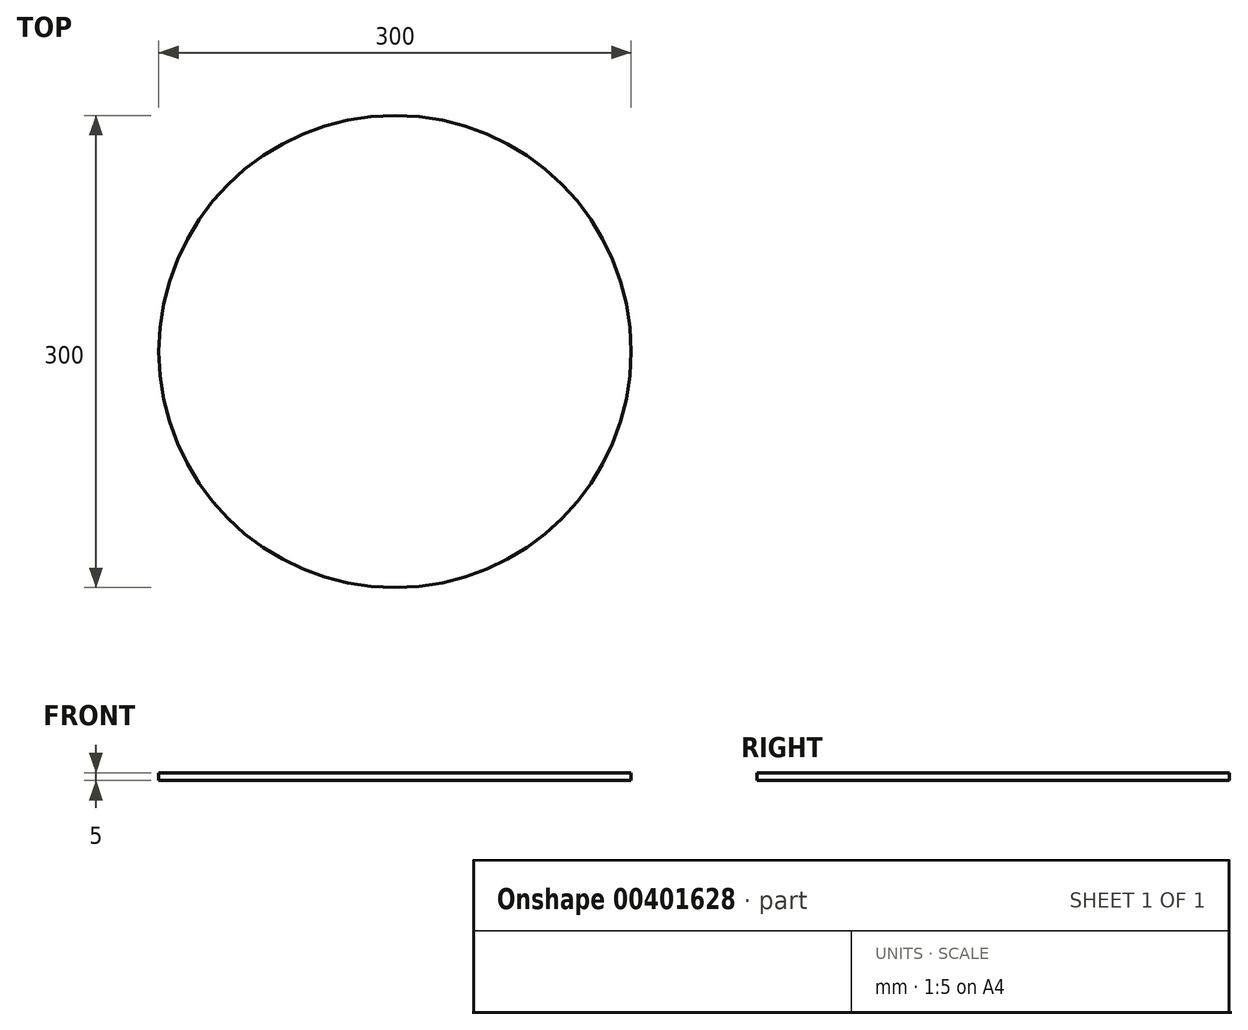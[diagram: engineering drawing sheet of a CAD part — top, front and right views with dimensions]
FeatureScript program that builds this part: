
annotation { "Feature Type Name" : "Feature", "Feature Type Description" : "" }
export const myFeature = defineFeature(function(context is Context, id is Id, definition is map)
    precondition{}
    {
        {
            var Q0;
            Q0=qCreatedBy(makeId("Top.planeOp"),FACE);
            var sketch = newSketch(context, id + "F0", { "sketchPlane" : qUnion([Q0])});
            skCircle(sketch, "E0", {"center": v(0, 0) * mm, "radius": 150 * mm});
            skSolve(sketch);
        }
        {
            var Q0;
            Q0=qSketchRegion(id+"F0",true);
            extrude(context, id + "F1", {"entities" : qUnion([Q0]), "depth" : 5 * mm});
        }
    });
